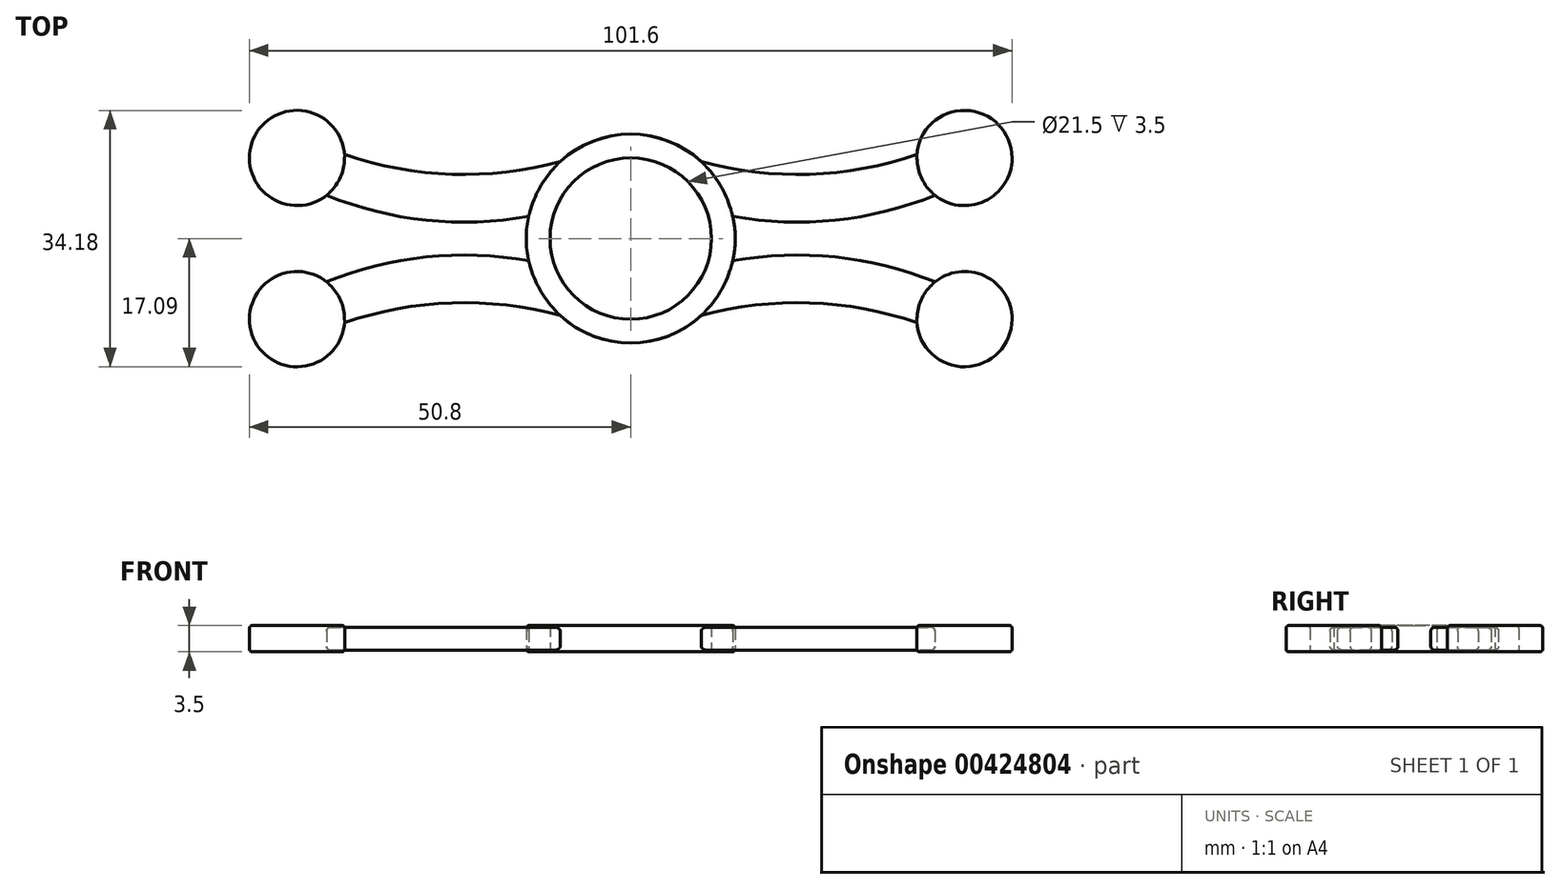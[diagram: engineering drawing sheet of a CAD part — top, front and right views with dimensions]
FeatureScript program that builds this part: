
annotation { "Feature Type Name" : "Feature", "Feature Type Description" : "" }
export const myFeature = defineFeature(function(context is Context, id is Id, definition is map)
    precondition{}
    {
        {
            var Q0;
            Q0=qCreatedBy(makeId("Top.planeOp"),FACE);
            var sketch = newSketch(context, id + "F0", { "sketchPlane" : qUnion([Q0])});
            skCircle(sketch, "E0", {"center": v(0, 0) * mm, "radius": 10.75 * mm});
            skCircle(sketch, "E1", {"center": v(0, 0) * mm, "radius": 13.92 * mm});
            skLineSegment(sketch, "E2", {"start": v(0, 0) * mm, "end": v(-44.45, 0) * mm});
            skLineSegment(sketch, "E3", {"start": v(0, 0) * mm, "end": v(44.45, 0) * mm});
            skLineSegment(sketch, "E4", {"start": v(-44.45, 10.74) * mm, "end": v(-44.45, -10.74) * mm});
            skLineSegment(sketch, "E5", {"start": v(44.45, 10.74) * mm, "end": v(44.45, -10.74) * mm});
            skPoint(sketch, "E6", {"position": v(-22.23, 0) * mm});
            skPoint(sketch, "E7", {"position": v(22.23, 0) * mm});
            skLineSegment(sketch, "E8", {"start": v(-22.23, 5.37) * mm, "end": v(-22.23, -5.37) * mm});
            skLineSegment(sketch, "E9", {"start": v(22.23, 5.37) * mm, "end": v(22.23, -5.37) * mm});
            skArc(sketch, "E10", {"start": v(-44.45, 10.74) * mm, "mid": v(-22.22, 5.37) * mm, "end": v(0, 10.75) * mm});
            skArc(sketch, "E11", {"start": v(0, 10.75) * mm, "mid": v(22.22, 5.37) * mm, "end": v(44.45, 10.74) * mm});
            skArc(sketch, "E12", {"start": v(0, -10.74) * mm, "mid": v(-22.23, -5.37) * mm, "end": v(-44.45, -10.74) * mm});
            skArc(sketch, "E13", {"start": v(44.45, -10.74) * mm, "mid": v(22.23, -5.37) * mm, "end": v(0, -10.74) * mm});
            skCircle(sketch, "E14", {"center": v(-44.45, 10.74) * mm, "radius": 6.35 * mm});
            skCircle(sketch, "E15", {"center": v(-44.45, -10.74) * mm, "radius": 6.35 * mm});
            skCircle(sketch, "E16", {"center": v(44.45, -10.74) * mm, "radius": 6.35 * mm});
            skCircle(sketch, "E17", {"center": v(44.45, 10.74) * mm, "radius": 6.35 * mm});
            skLineSegment(sketch, "E18", {"start": v(-44.45, 10.74) * mm, "end": v(-44.45, 13.92) * mm});
            skLineSegment(sketch, "E19", {"start": v(-44.45, -10.74) * mm, "end": v(-44.45, -13.92) * mm});
            skLineSegment(sketch, "E20", {"start": v(44.45, -10.74) * mm, "end": v(44.45, -13.92) * mm});
            skLineSegment(sketch, "E21", {"start": v(44.45, 10.74) * mm, "end": v(44.45, 13.92) * mm});
            skPoint(sketch, "E22", {"position": v(-44.45, 7.57) * mm});
            skPoint(sketch, "E23", {"position": v(-22.23, 2.2) * mm});
            skPoint(sketch, "E24", {"position": v(22.23, 2.2) * mm});
            skPoint(sketch, "E25", {"position": v(44.45, 7.57) * mm});
            skPoint(sketch, "E26", {"position": v(44.45, -7.57) * mm});
            skPoint(sketch, "E27", {"position": v(22.23, -2.2) * mm});
            skPoint(sketch, "E28", {"position": v(-22.23, -2.2) * mm});
            skPoint(sketch, "E29", {"position": v(-44.45, -7.57) * mm});
            skLineSegment(sketch, "E30", {"start": v(0, -10.74) * mm, "end": v(0, -7.57) * mm});
            skLineSegment(sketch, "E31", {"start": v(0, 10.75) * mm, "end": v(0, 7.58) * mm});
            skLineSegment(sketch, "E32", {"start": v(-22.23, 5.37) * mm, "end": v(-22.23, 8.55) * mm});
            skLineSegment(sketch, "E33", {"start": v(-22.23, -5.37) * mm, "end": v(-22.23, -8.55) * mm});
            skLineSegment(sketch, "E34", {"start": v(22.23, -5.37) * mm, "end": v(22.23, -8.55) * mm});
            skLineSegment(sketch, "E35", {"start": v(22.23, 5.37) * mm, "end": v(22.23, 8.55) * mm});
            skArc(sketch, "E36", {"start": v(-44.45, 13.92) * mm, "mid": v(-22.22, 8.55) * mm, "end": v(0, 13.92) * mm});
            skArc(sketch, "E37", {"start": v(0, -13.92) * mm, "mid": v(-22.22, -8.55) * mm, "end": v(-44.45, -13.92) * mm});
            skArc(sketch, "E38", {"start": v(0, -7.57) * mm, "mid": v(-22.23, -2.2) * mm, "end": v(-44.45, -7.57) * mm});
            skArc(sketch, "E39", {"start": v(-44.45, 7.57) * mm, "mid": v(-22.22, 2.2) * mm, "end": v(0, 7.58) * mm});
            skArc(sketch, "E40", {"start": v(0, 13.92) * mm, "mid": v(22.22, 8.55) * mm, "end": v(44.45, 13.92) * mm});
            skArc(sketch, "E41", {"start": v(0, 7.58) * mm, "mid": v(22.22, 2.2) * mm, "end": v(44.45, 7.57) * mm});
            skArc(sketch, "E42", {"start": v(44.45, -7.57) * mm, "mid": v(22.22, -2.2) * mm, "end": v(0, -7.57) * mm});
            skArc(sketch, "E43", {"start": v(44.45, -13.92) * mm, "mid": v(22.23, -8.55) * mm, "end": v(0, -13.92) * mm});
            skSolve(sketch);
        }
        {
            var Q0;
            {var subQ0=sQuery(id+"F0.wireOp",EDGE,"E36");var subQ1=sQuery(id+"F0.wireOp",EDGE,"E1");var subQ3=makeQuery(id+"F0.imprint","INTERSECT",VERTEX,{"derivedFrom":[subQ1,subQ0]});Q0=makeQuery(id+"F0.imprint","IMPRINT",FACE,{"disambiguationData":[TD([[makeQuery(id+"F0.imprint","IMPRINT",EDGE,{"disambiguationData":[TD([[subQ3,1.0]])],"derivedFrom":subQ1}),1.0]])]});}
            var Q1;
            {var subQ1=sQuery(id+"F0.wireOp",EDGE,"E1");var subQ5=sQuery(id+"F0.wireOp",EDGE,"E40");var subQ7=makeQuery(id+"F0.imprint","INTERSECT",VERTEX,{"derivedFrom":[subQ1,subQ5]});Q1=makeQuery(id+"F0.imprint","IMPRINT",FACE,{"disambiguationData":[TD([[makeQuery(id+"F0.imprint","IMPRINT",EDGE,{"disambiguationData":[TD([[subQ7,1.0]])],"derivedFrom":subQ1}),1.0]])]});}
            var Q2;
            {var subQ0=sQuery(id+"F0.wireOp",EDGE,"E10");var subQ1=sQuery(id+"F0.wireOp",EDGE,"E0");var subQ2=makeQuery(id+"F0.imprint","INTERSECT",VERTEX,{"derivedFrom":[subQ1,subQ0]});Q2=makeQuery(id+"F0.imprint","IMPRINT",FACE,{"disambiguationData":[TD([[makeQuery(id+"F0.imprint","IMPRINT",EDGE,{"disambiguationData":[TD([[subQ2,-1.0]])],"derivedFrom":subQ1}),-1.0]])]});}
            var Q3;
            {var subQ0=sQuery(id+"F0.wireOp",EDGE,"E40");var subQ1=sQuery(id+"F0.wireOp",EDGE,"E1");var subQ3=makeQuery(id+"F0.imprint","INTERSECT",VERTEX,{"derivedFrom":[subQ1,subQ0]});Q3=makeQuery(id+"F0.imprint","IMPRINT",FACE,{"disambiguationData":[TD([[makeQuery(id+"F0.imprint","IMPRINT",EDGE,{"disambiguationData":[TD([[subQ3,-1.0]])],"derivedFrom":subQ1}),1.0]])]});}
            var Q4;
            {var subQ0=sQuery(id+"F0.wireOp",EDGE,"E41");var subQ1=sQuery(id+"F0.wireOp",EDGE,"E0");var subQ2=makeQuery(id+"F0.imprint","INTERSECT",VERTEX,{"derivedFrom":[subQ1,subQ0]});Q4=makeQuery(id+"F0.imprint","IMPRINT",FACE,{"disambiguationData":[TD([[makeQuery(id+"F0.imprint","IMPRINT",EDGE,{"disambiguationData":[TD([[subQ2,-1.0]])],"derivedFrom":subQ1}),-1.0]])]});}
            var Q5;
            {var subQ0=sQuery(id+"F0.wireOp",EDGE,"E41");var subQ1=sQuery(id+"F0.wireOp",EDGE,"E0");var subQ2=makeQuery(id+"F0.imprint","INTERSECT",VERTEX,{"derivedFrom":[subQ1,subQ0]});Q5=makeQuery(id+"F0.imprint","IMPRINT",FACE,{"disambiguationData":[TD([[makeQuery(id+"F0.imprint","IMPRINT",EDGE,{"disambiguationData":[TD([[subQ2,1.0]])],"derivedFrom":subQ1}),-1.0]])]});}
            var Q6;
            {var subQ0=sQuery(id+"F0.wireOp",EDGE,"E39");var subQ1=sQuery(id+"F0.wireOp",EDGE,"E0");var subQ2=makeQuery(id+"F0.imprint","INTERSECT",VERTEX,{"derivedFrom":[subQ1,subQ0]});Q6=makeQuery(id+"F0.imprint","IMPRINT",FACE,{"disambiguationData":[TD([[makeQuery(id+"F0.imprint","IMPRINT",EDGE,{"disambiguationData":[TD([[subQ2,-1.0]])],"derivedFrom":subQ1}),-1.0]])]});}
            var Q7;
            {var subQ0=sQuery(id+"F0.wireOp",EDGE,"E2");var subQ1=sQuery(id+"F0.wireOp",EDGE,"E0");var subQ2=makeQuery(id+"F0.imprint","INTERSECT",VERTEX,{"derivedFrom":[subQ1,subQ0]});Q7=makeQuery(id+"F0.imprint","IMPRINT",FACE,{"disambiguationData":[TD([[makeQuery(id+"F0.imprint","IMPRINT",EDGE,{"disambiguationData":[TD([[subQ2,-1.0]])],"derivedFrom":subQ1}),-1.0]])]});}
            var Q8;
            {var subQ0=sQuery(id+"F0.wireOp",EDGE,"E38");var subQ1=sQuery(id+"F0.wireOp",EDGE,"E0");var subQ2=makeQuery(id+"F0.imprint","INTERSECT",VERTEX,{"derivedFrom":[subQ1,subQ0]});Q8=makeQuery(id+"F0.imprint","IMPRINT",FACE,{"disambiguationData":[TD([[makeQuery(id+"F0.imprint","IMPRINT",EDGE,{"disambiguationData":[TD([[subQ2,-1.0]])],"derivedFrom":subQ1}),-1.0]])]});}
            var Q9;
            {var subQ5=sQuery(id+"F0.wireOp",EDGE,"E12");var subQ6=sQuery(id+"F0.wireOp",EDGE,"E0");var subQ7=makeQuery(id+"F0.imprint","INTERSECT",VERTEX,{"derivedFrom":[subQ6,subQ5]});Q9=makeQuery(id+"F0.imprint","IMPRINT",FACE,{"disambiguationData":[TD([[makeQuery(id+"F0.imprint","IMPRINT",EDGE,{"disambiguationData":[TD([[subQ7,-1.0]])],"derivedFrom":subQ6}),-1.0]])]});}
            var Q10;
            {var subQ0=sQuery(id+"F0.wireOp",EDGE,"E37");var subQ1=sQuery(id+"F0.wireOp",EDGE,"E1");var subQ3=makeQuery(id+"F0.imprint","INTERSECT",VERTEX,{"derivedFrom":[subQ1,subQ0]});Q10=makeQuery(id+"F0.imprint","IMPRINT",FACE,{"disambiguationData":[TD([[makeQuery(id+"F0.imprint","IMPRINT",EDGE,{"disambiguationData":[TD([[subQ3,-1.0]])],"derivedFrom":subQ1}),1.0]])]});}
            var Q11;
            {var subQ0=sQuery(id+"F0.wireOp",EDGE,"E43");var subQ1=sQuery(id+"F0.wireOp",EDGE,"E1");var subQ3=makeQuery(id+"F0.imprint","INTERSECT",VERTEX,{"derivedFrom":[subQ1,subQ0]});Q11=makeQuery(id+"F0.imprint","IMPRINT",FACE,{"disambiguationData":[TD([[makeQuery(id+"F0.imprint","IMPRINT",EDGE,{"disambiguationData":[TD([[subQ3,1.0]])],"derivedFrom":subQ1}),1.0]])]});}
            var Q12;
            {var subQ0=sQuery(id+"F0.wireOp",EDGE,"E13");var subQ1=sQuery(id+"F0.wireOp",EDGE,"E0");var subQ2=makeQuery(id+"F0.imprint","INTERSECT",VERTEX,{"derivedFrom":[subQ1,subQ0]});Q12=makeQuery(id+"F0.imprint","IMPRINT",FACE,{"disambiguationData":[TD([[makeQuery(id+"F0.imprint","IMPRINT",EDGE,{"disambiguationData":[TD([[subQ2,-1.0]])],"derivedFrom":subQ1}),-1.0]])]});}
            var Q13;
            {var subQ0=sQuery(id+"F0.wireOp",EDGE,"E3");var subQ1=sQuery(id+"F0.wireOp",EDGE,"E0");var subQ2=makeQuery(id+"F0.imprint","INTERSECT",VERTEX,{"derivedFrom":[subQ1,subQ0]});Q13=makeQuery(id+"F0.imprint","IMPRINT",FACE,{"disambiguationData":[TD([[makeQuery(id+"F0.imprint","IMPRINT",EDGE,{"disambiguationData":[TD([[subQ2,1.0]])],"derivedFrom":subQ1}),-1.0]])]});}
            extrude(context, id + "F1", {"entities" : qUnion([Q0, Q1, Q2, Q3, Q4, Q5, Q6, Q7, Q8, Q9, Q10, Q11, Q12, Q13]), "endBound" : BoundingType.SYMMETRIC, "depth" : 3.5 * mm});
        }
        {
            var Q0;
            {var subQ0=sQuery(id+"F0.wireOp",EDGE,"E10");var subQ1=sQuery(id+"F0.wireOp",EDGE,"E1");var subQ2=makeQuery(id+"F0.imprint","INTERSECT",VERTEX,{"derivedFrom":[subQ1,subQ0]});Q0=makeQuery(id+"F0.imprint","IMPRINT",FACE,{"disambiguationData":[TD([[makeQuery(id+"F0.imprint","IMPRINT",EDGE,{"disambiguationData":[TD([[subQ2,-1.0]])],"derivedFrom":subQ1}),-1.0]])]});}
            var Q1;
            {var subQ5=sQuery(id+"F0.wireOp",EDGE,"E32");Q1=makeQuery(id+"F0.imprint","IMPRINT",FACE,{"disambiguationData":[TD([[makeQuery(id+"F0.imprint","IMPRINT",EDGE,{"derivedFrom":subQ5}),-1.0]])]});}
            var Q2;
            {var subQ0=sQuery(id+"F0.wireOp",EDGE,"E32");Q2=makeQuery(id+"F0.imprint","IMPRINT",FACE,{"disambiguationData":[TD([[makeQuery(id+"F0.imprint","IMPRINT",EDGE,{"derivedFrom":subQ0}),1.0]])]});}
            var Q3;
            {var subQ0=sQuery(id+"F0.wireOp",EDGE,"E10");var subQ5=sQuery(id+"F0.wireOp",EDGE,"E14");var subQ6=makeQuery(id+"F0.imprint","INTERSECT",VERTEX,{"derivedFrom":[subQ0,subQ5]});Q3=makeQuery(id+"F0.imprint","IMPRINT",FACE,{"disambiguationData":[TD([[makeQuery(id+"F0.imprint","IMPRINT",EDGE,{"disambiguationData":[TD([[subQ6,1.0]])],"derivedFrom":subQ5}),-1.0]])]});}
            var Q4;
            {var subQ0=sQuery(id+"F0.wireOp",EDGE,"E41");var subQ1=sQuery(id+"F0.wireOp",EDGE,"E1");var subQ2=makeQuery(id+"F0.imprint","INTERSECT",VERTEX,{"derivedFrom":[subQ1,subQ0]});Q4=makeQuery(id+"F0.imprint","IMPRINT",FACE,{"disambiguationData":[TD([[makeQuery(id+"F0.imprint","IMPRINT",EDGE,{"disambiguationData":[TD([[subQ2,-1.0]])],"derivedFrom":subQ1}),-1.0]])]});}
            var Q5;
            {var subQ5=sQuery(id+"F0.wireOp",EDGE,"E35");Q5=makeQuery(id+"F0.imprint","IMPRINT",FACE,{"disambiguationData":[TD([[makeQuery(id+"F0.imprint","IMPRINT",EDGE,{"derivedFrom":subQ5}),1.0]])]});}
            var Q6;
            {var subQ0=sQuery(id+"F0.wireOp",EDGE,"E11");var subQ5=sQuery(id+"F0.wireOp",EDGE,"E17");var subQ7=makeQuery(id+"F0.imprint","INTERSECT",VERTEX,{"derivedFrom":[subQ0,subQ5]});Q6=makeQuery(id+"F0.imprint","IMPRINT",FACE,{"disambiguationData":[TD([[makeQuery(id+"F0.imprint","IMPRINT",EDGE,{"disambiguationData":[TD([[subQ7,-1.0]])],"derivedFrom":subQ5}),-1.0]])]});}
            var Q7;
            {var subQ0=sQuery(id+"F0.wireOp",EDGE,"E35");Q7=makeQuery(id+"F0.imprint","IMPRINT",FACE,{"disambiguationData":[TD([[makeQuery(id+"F0.imprint","IMPRINT",EDGE,{"derivedFrom":subQ0}),-1.0]])]});}
            var Q8;
            {var subQ0=sQuery(id+"F0.wireOp",EDGE,"E13");var subQ5=sQuery(id+"F0.wireOp",EDGE,"E16");var subQ6=makeQuery(id+"F0.imprint","INTERSECT",VERTEX,{"derivedFrom":[subQ0,subQ5]});Q8=makeQuery(id+"F0.imprint","IMPRINT",FACE,{"disambiguationData":[TD([[makeQuery(id+"F0.imprint","IMPRINT",EDGE,{"disambiguationData":[TD([[subQ6,1.0]])],"derivedFrom":subQ5}),-1.0]])]});}
            var Q9;
            {var subQ0=sQuery(id+"F0.wireOp",EDGE,"E34");Q9=makeQuery(id+"F0.imprint","IMPRINT",FACE,{"disambiguationData":[TD([[makeQuery(id+"F0.imprint","IMPRINT",EDGE,{"derivedFrom":subQ0}),1.0]])]});}
            var Q10;
            {var subQ0=sQuery(id+"F0.wireOp",EDGE,"E13");var subQ1=sQuery(id+"F0.wireOp",EDGE,"E1");var subQ2=makeQuery(id+"F0.imprint","INTERSECT",VERTEX,{"derivedFrom":[subQ1,subQ0]});Q10=makeQuery(id+"F0.imprint","IMPRINT",FACE,{"disambiguationData":[TD([[makeQuery(id+"F0.imprint","IMPRINT",EDGE,{"disambiguationData":[TD([[subQ2,-1.0]])],"derivedFrom":subQ1}),-1.0]])]});}
            var Q11;
            {var subQ5=sQuery(id+"F0.wireOp",EDGE,"E33");Q11=makeQuery(id+"F0.imprint","IMPRINT",FACE,{"disambiguationData":[TD([[makeQuery(id+"F0.imprint","IMPRINT",EDGE,{"derivedFrom":subQ5}),1.0]])]});}
            var Q12;
            {var subQ0=sQuery(id+"F0.wireOp",EDGE,"E38");var subQ1=sQuery(id+"F0.wireOp",EDGE,"E1");var subQ2=makeQuery(id+"F0.imprint","INTERSECT",VERTEX,{"derivedFrom":[subQ1,subQ0]});Q12=makeQuery(id+"F0.imprint","IMPRINT",FACE,{"disambiguationData":[TD([[makeQuery(id+"F0.imprint","IMPRINT",EDGE,{"disambiguationData":[TD([[subQ2,-1.0]])],"derivedFrom":subQ1}),-1.0]])]});}
            var Q13;
            {var subQ0=sQuery(id+"F0.wireOp",EDGE,"E33");Q13=makeQuery(id+"F0.imprint","IMPRINT",FACE,{"disambiguationData":[TD([[makeQuery(id+"F0.imprint","IMPRINT",EDGE,{"derivedFrom":subQ0}),-1.0]])]});}
            var Q14;
            {var subQ0=sQuery(id+"F0.wireOp",EDGE,"E12");var subQ5=sQuery(id+"F0.wireOp",EDGE,"E15");var subQ6=makeQuery(id+"F0.imprint","INTERSECT",VERTEX,{"derivedFrom":[subQ0,subQ5]});Q14=makeQuery(id+"F0.imprint","IMPRINT",FACE,{"disambiguationData":[TD([[makeQuery(id+"F0.imprint","IMPRINT",EDGE,{"disambiguationData":[TD([[subQ6,-1.0]])],"derivedFrom":subQ5}),-1.0]])]});}
            var Q15;
            {var subQ5=sQuery(id+"F0.wireOp",EDGE,"E34");Q15=makeQuery(id+"F0.imprint","IMPRINT",FACE,{"disambiguationData":[TD([[makeQuery(id+"F0.imprint","IMPRINT",EDGE,{"derivedFrom":subQ5}),-1.0]])]});}
            extrude(context, id + "F2", {"entities" : qUnion([Q0, Q1, Q2, Q3, Q4, Q5, Q6, Q7, Q8, Q9, Q10, Q11, Q12, Q13, Q14, Q15]), "operationType" : NewBodyOperationType.ADD, "endBound" : BoundingType.SYMMETRIC, "depth" : 3.05 * mm});
        }
        {
            var Q0;
            {var subQ0=sQuery(id+"F0.wireOp",EDGE,"E21");Q0=makeQuery(id+"F0.imprint","IMPRINT",FACE,{"disambiguationData":[TD([[makeQuery(id+"F0.imprint","IMPRINT",EDGE,{"derivedFrom":subQ0}),-1.0]])]});}
            var Q1;
            {var subQ0=sQuery(id+"F0.wireOp",EDGE,"E41");var subQ1=sQuery(id+"F0.wireOp",EDGE,"E5");var subQ2=makeQuery(id+"F0.imprint","INTERSECT",VERTEX,{"derivedFrom":[subQ1,subQ0]});Q1=makeQuery(id+"F0.imprint","IMPRINT",FACE,{"disambiguationData":[TD([[makeQuery(id+"F0.imprint","IMPRINT",EDGE,{"disambiguationData":[TD([[subQ2,-1.0]])],"derivedFrom":subQ1}),-1.0]])]});}
            var Q2;
            {var subQ0=sQuery(id+"F0.wireOp",EDGE,"E11");var subQ5=sQuery(id+"F0.wireOp",EDGE,"E17");var subQ6=makeQuery(id+"F0.imprint","INTERSECT",VERTEX,{"derivedFrom":[subQ0,subQ5]});Q2=makeQuery(id+"F0.imprint","IMPRINT",FACE,{"disambiguationData":[TD([[makeQuery(id+"F0.imprint","IMPRINT",EDGE,{"disambiguationData":[TD([[subQ6,-1.0]])],"derivedFrom":subQ5}),1.0]])]});}
            var Q3;
            {var subQ0=sQuery(id+"F0.wireOp",EDGE,"E21");Q3=makeQuery(id+"F0.imprint","IMPRINT",FACE,{"disambiguationData":[TD([[makeQuery(id+"F0.imprint","IMPRINT",EDGE,{"derivedFrom":subQ0}),1.0]])]});}
            var Q4;
            {var subQ0=sQuery(id+"F0.wireOp",EDGE,"E20");Q4=makeQuery(id+"F0.imprint","IMPRINT",FACE,{"disambiguationData":[TD([[makeQuery(id+"F0.imprint","IMPRINT",EDGE,{"derivedFrom":subQ0}),1.0]])]});}
            var Q5;
            {var subQ0=sQuery(id+"F0.wireOp",EDGE,"E20");Q5=makeQuery(id+"F0.imprint","IMPRINT",FACE,{"disambiguationData":[TD([[makeQuery(id+"F0.imprint","IMPRINT",EDGE,{"derivedFrom":subQ0}),-1.0]])]});}
            var Q6;
            {var subQ0=sQuery(id+"F0.wireOp",EDGE,"E13");var subQ5=sQuery(id+"F0.wireOp",EDGE,"E16");var subQ6=makeQuery(id+"F0.imprint","INTERSECT",VERTEX,{"derivedFrom":[subQ0,subQ5]});Q6=makeQuery(id+"F0.imprint","IMPRINT",FACE,{"disambiguationData":[TD([[makeQuery(id+"F0.imprint","IMPRINT",EDGE,{"disambiguationData":[TD([[subQ6,1.0]])],"derivedFrom":subQ5}),1.0]])]});}
            var Q7;
            {var subQ0=sQuery(id+"F0.wireOp",EDGE,"E42");var subQ1=sQuery(id+"F0.wireOp",EDGE,"E5");var subQ2=makeQuery(id+"F0.imprint","INTERSECT",VERTEX,{"derivedFrom":[subQ1,subQ0]});Q7=makeQuery(id+"F0.imprint","IMPRINT",FACE,{"disambiguationData":[TD([[makeQuery(id+"F0.imprint","IMPRINT",EDGE,{"disambiguationData":[TD([[subQ2,1.0]])],"derivedFrom":subQ1}),-1.0]])]});}
            var Q8;
            {var subQ0=sQuery(id+"F0.wireOp",EDGE,"E19");Q8=makeQuery(id+"F0.imprint","IMPRINT",FACE,{"disambiguationData":[TD([[makeQuery(id+"F0.imprint","IMPRINT",EDGE,{"derivedFrom":subQ0}),-1.0]])]});}
            var Q9;
            {var subQ0=sQuery(id+"F0.wireOp",EDGE,"E19");Q9=makeQuery(id+"F0.imprint","IMPRINT",FACE,{"disambiguationData":[TD([[makeQuery(id+"F0.imprint","IMPRINT",EDGE,{"derivedFrom":subQ0}),1.0]])]});}
            var Q10;
            {var subQ0=sQuery(id+"F0.wireOp",EDGE,"E12");var subQ5=sQuery(id+"F0.wireOp",EDGE,"E15");var subQ6=makeQuery(id+"F0.imprint","INTERSECT",VERTEX,{"derivedFrom":[subQ0,subQ5]});Q10=makeQuery(id+"F0.imprint","IMPRINT",FACE,{"disambiguationData":[TD([[makeQuery(id+"F0.imprint","IMPRINT",EDGE,{"disambiguationData":[TD([[subQ6,-1.0]])],"derivedFrom":subQ5}),1.0]])]});}
            var Q11;
            {var subQ0=sQuery(id+"F0.wireOp",EDGE,"E38");var subQ1=sQuery(id+"F0.wireOp",EDGE,"E4");var subQ2=makeQuery(id+"F0.imprint","INTERSECT",VERTEX,{"derivedFrom":[subQ1,subQ0]});Q11=makeQuery(id+"F0.imprint","IMPRINT",FACE,{"disambiguationData":[TD([[makeQuery(id+"F0.imprint","IMPRINT",EDGE,{"disambiguationData":[TD([[subQ2,1.0]])],"derivedFrom":subQ1}),1.0]])]});}
            var Q12;
            {var subQ0=sQuery(id+"F0.wireOp",EDGE,"E18");Q12=makeQuery(id+"F0.imprint","IMPRINT",FACE,{"disambiguationData":[TD([[makeQuery(id+"F0.imprint","IMPRINT",EDGE,{"derivedFrom":subQ0}),1.0]])]});}
            var Q13;
            {var subQ0=sQuery(id+"F0.wireOp",EDGE,"E10");var subQ5=sQuery(id+"F0.wireOp",EDGE,"E14");var subQ6=makeQuery(id+"F0.imprint","INTERSECT",VERTEX,{"derivedFrom":[subQ0,subQ5]});Q13=makeQuery(id+"F0.imprint","IMPRINT",FACE,{"disambiguationData":[TD([[makeQuery(id+"F0.imprint","IMPRINT",EDGE,{"disambiguationData":[TD([[subQ6,1.0]])],"derivedFrom":subQ5}),1.0]])]});}
            var Q14;
            {var subQ0=sQuery(id+"F0.wireOp",EDGE,"E39");var subQ1=sQuery(id+"F0.wireOp",EDGE,"E4");var subQ2=makeQuery(id+"F0.imprint","INTERSECT",VERTEX,{"derivedFrom":[subQ1,subQ0]});Q14=makeQuery(id+"F0.imprint","IMPRINT",FACE,{"disambiguationData":[TD([[makeQuery(id+"F0.imprint","IMPRINT",EDGE,{"disambiguationData":[TD([[subQ2,-1.0]])],"derivedFrom":subQ1}),1.0]])]});}
            var Q15;
            {var subQ0=sQuery(id+"F0.wireOp",EDGE,"E18");Q15=makeQuery(id+"F0.imprint","IMPRINT",FACE,{"disambiguationData":[TD([[makeQuery(id+"F0.imprint","IMPRINT",EDGE,{"derivedFrom":subQ0}),-1.0]])]});}
            extrude(context, id + "F3", {"entities" : qUnion([Q0, Q1, Q2, Q3, Q4, Q5, Q6, Q7, Q8, Q9, Q10, Q11, Q12, Q13, Q14, Q15]), "operationType" : NewBodyOperationType.ADD, "endBound" : BoundingType.SYMMETRIC, "depth" : 3.5 * mm});
        }
        {
            var Q0;
            Q0=makeQuery(id+"F3.opExtrude","CAP_EDGE",EDGE,{"disambiguationData":[OSD([sQuery(id+"F0.wireOp",EDGE,"E14")])],"isStart":false});
            var Q1;
            Q1=makeQuery(id+"F3.opExtrude","CAP_EDGE",EDGE,{"disambiguationData":[OSD([sQuery(id+"F0.wireOp",EDGE,"E14")])],"isStart":true});
            var Q2;
            Q2=makeQuery(id+"F3.opExtrude","CAP_EDGE",EDGE,{"disambiguationData":[OSD([sQuery(id+"F0.wireOp",EDGE,"E15")])],"isStart":false});
            var Q3;
            Q3=makeQuery(id+"F3.opExtrude","CAP_EDGE",EDGE,{"disambiguationData":[OSD([sQuery(id+"F0.wireOp",EDGE,"E15")])],"isStart":true});
            var Q4;
            Q4=makeQuery(id+"F3.opExtrude","CAP_EDGE",EDGE,{"disambiguationData":[OSD([sQuery(id+"F0.wireOp",EDGE,"E16")])],"isStart":false});
            var Q5;
            Q5=makeQuery(id+"F3.opExtrude","CAP_EDGE",EDGE,{"disambiguationData":[OSD([sQuery(id+"F0.wireOp",EDGE,"E16")])],"isStart":true});
            var Q6;
            Q6=makeQuery(id+"F3.opExtrude","CAP_EDGE",EDGE,{"disambiguationData":[OSD([sQuery(id+"F0.wireOp",EDGE,"E17")])],"isStart":false});
            var Q7;
            Q7=makeQuery(id+"F3.opExtrude","CAP_EDGE",EDGE,{"disambiguationData":[OSD([sQuery(id+"F0.wireOp",EDGE,"E17")])],"isStart":true});
            var Q8;
            Q8=makeQuery(id+"F1.opExtrude","CAP_EDGE",EDGE,{"disambiguationData":[OSD([sQuery(id+"F0.wireOp",EDGE,"E1")])],"isStart":false});
            var Q9;
            Q9=makeQuery(id+"F1.opExtrude","CAP_EDGE",EDGE,{"disambiguationData":[OSD([sQuery(id+"F0.wireOp",EDGE,"E1")])],"isStart":true});
            fillet(context, id + "F4", {"entities" : qUnion([Q0, Q1, Q2, Q3, Q4, Q5, Q6, Q7, Q8, Q9]), "radius" : 0.38 * mm, "tangentPropagation" : true, "allowEdgeOverflow" : false});
        }
        {
            var Q0;
            Q0=makeQuery(id+"F2.opExtrude","CAP_EDGE",EDGE,{"disambiguationData":[OSD([sQuery(id+"F0.wireOp",EDGE,"E43")])],"isStart":false});
            var Q1;
            Q1=makeQuery(id+"F2.opExtrude","CAP_EDGE",EDGE,{"disambiguationData":[OSD([sQuery(id+"F0.wireOp",EDGE,"E43")])],"isStart":true});
            var Q2;
            Q2=makeQuery(id+"F2.opExtrude","CAP_EDGE",EDGE,{"disambiguationData":[OSD([sQuery(id+"F0.wireOp",EDGE,"E42")])],"isStart":false});
            var Q3;
            Q3=makeQuery(id+"F2.opExtrude","CAP_EDGE",EDGE,{"disambiguationData":[OSD([sQuery(id+"F0.wireOp",EDGE,"E37")])],"isStart":false});
            var Q4;
            Q4=makeQuery(id+"F2.opExtrude","CAP_EDGE",EDGE,{"disambiguationData":[OSD([sQuery(id+"F0.wireOp",EDGE,"E37")])],"isStart":true});
            var Q5;
            Q5=makeQuery(id+"F2.opExtrude","CAP_EDGE",EDGE,{"disambiguationData":[OSD([sQuery(id+"F0.wireOp",EDGE,"E38")])],"isStart":true});
            var Q6;
            Q6=makeQuery(id+"F2.opExtrude","CAP_EDGE",EDGE,{"disambiguationData":[OSD([sQuery(id+"F0.wireOp",EDGE,"E39")])],"isStart":true});
            var Q7;
            Q7=makeQuery(id+"F2.opExtrude","CAP_EDGE",EDGE,{"disambiguationData":[OSD([sQuery(id+"F0.wireOp",EDGE,"E39")])],"isStart":false});
            var Q8;
            Q8=makeQuery(id+"F2.opExtrude","CAP_EDGE",EDGE,{"disambiguationData":[OSD([sQuery(id+"F0.wireOp",EDGE,"E38")])],"isStart":false});
            var Q9;
            Q9=makeQuery(id+"F2.opExtrude","CAP_EDGE",EDGE,{"disambiguationData":[OSD([sQuery(id+"F0.wireOp",EDGE,"E42")])],"isStart":true});
            var Q10;
            Q10=makeQuery(id+"F2.opExtrude","CAP_EDGE",EDGE,{"disambiguationData":[OSD([sQuery(id+"F0.wireOp",EDGE,"E36")])],"isStart":true});
            var Q11;
            Q11=makeQuery(id+"F2.opExtrude","CAP_EDGE",EDGE,{"disambiguationData":[OSD([sQuery(id+"F0.wireOp",EDGE,"E36")])],"isStart":false});
            var Q12;
            Q12=makeQuery(id+"F2.opExtrude","CAP_EDGE",EDGE,{"disambiguationData":[OSD([sQuery(id+"F0.wireOp",EDGE,"E40")])],"isStart":true});
            var Q13;
            Q13=makeQuery(id+"F2.opExtrude","CAP_EDGE",EDGE,{"disambiguationData":[OSD([sQuery(id+"F0.wireOp",EDGE,"E40")])],"isStart":false});
            var Q14;
            Q14=makeQuery(id+"F2.opExtrude","CAP_EDGE",EDGE,{"disambiguationData":[OSD([sQuery(id+"F0.wireOp",EDGE,"E41")])],"isStart":false});
            var Q15;
            Q15=makeQuery(id+"F2.opExtrude","CAP_EDGE",EDGE,{"disambiguationData":[OSD([sQuery(id+"F0.wireOp",EDGE,"E41")])],"isStart":true});
            fillet(context, id + "F5", {"entities" : qUnion([Q0, Q1, Q2, Q3, Q4, Q5, Q6, Q7, Q8, Q9, Q10, Q11, Q12, Q13, Q14, Q15]), "radius" : 0.5 * mm, "tangentPropagation" : true, "allowEdgeOverflow" : false});
        }
    });
